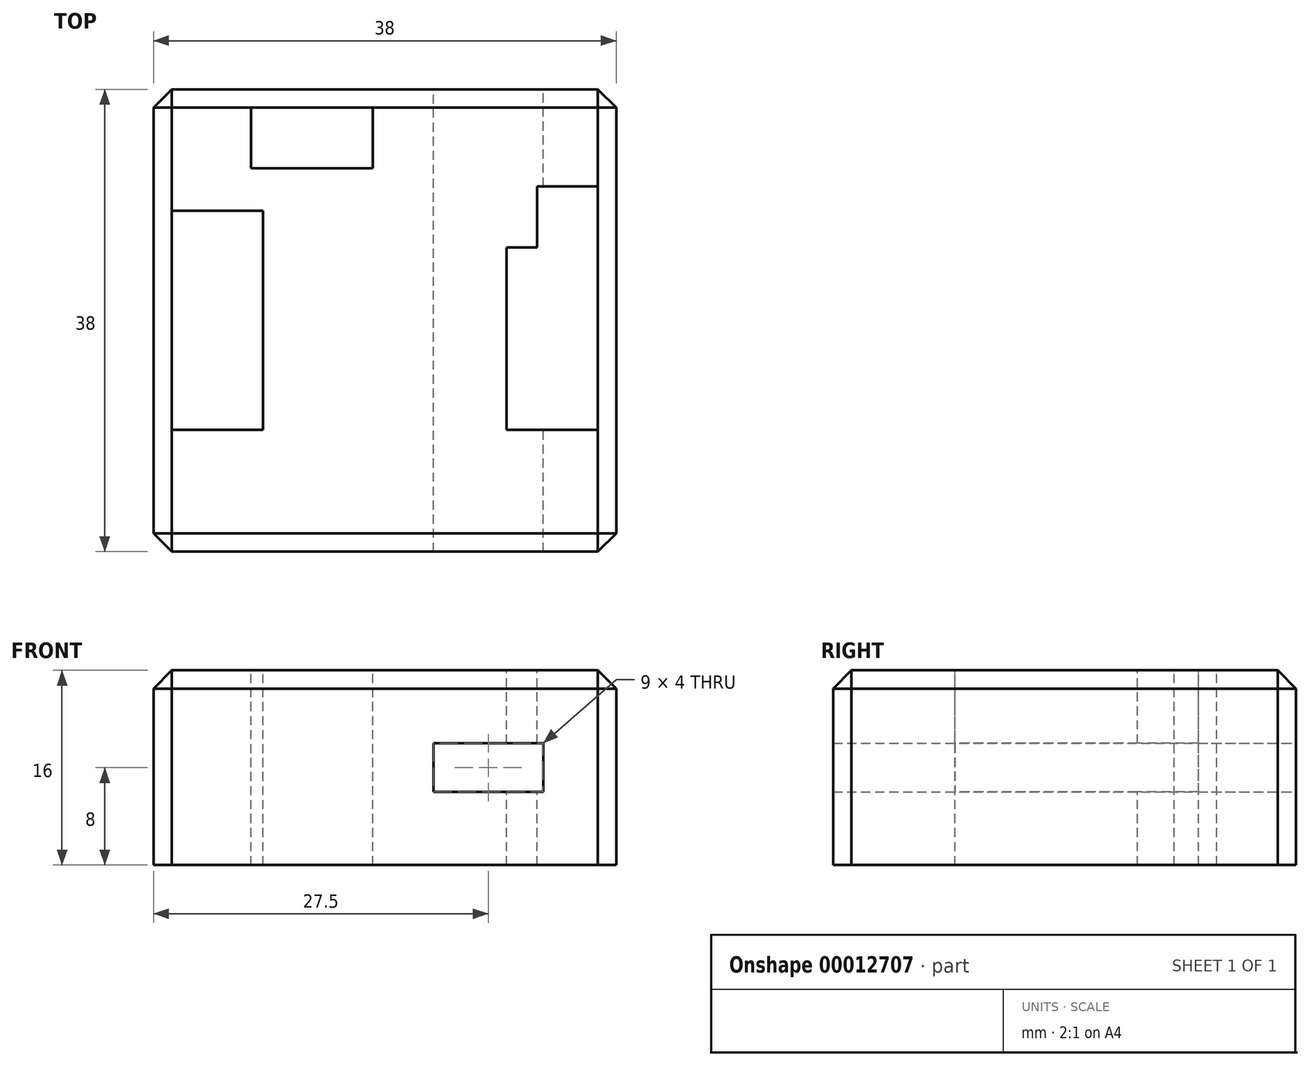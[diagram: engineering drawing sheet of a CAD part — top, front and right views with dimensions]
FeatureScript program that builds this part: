
annotation { "Feature Type Name" : "Feature", "Feature Type Description" : "" }
export const myFeature = defineFeature(function(context is Context, id is Id, definition is map)
    precondition{}
    {
        {
            var Q0;
            Q0=qCreatedBy(makeId("Top.planeOp"),FACE);
            var sketch = newSketch(context, id + "F0", { "sketchPlane" : qUnion([Q0])});
            skLineSegment(sketch, "E0.rect.bottom", {"start": v(19, 19) * mm, "end": v(-19, 19) * mm});
            skLineSegment(sketch, "E0.rect.top", {"start": v(19, -19) * mm, "end": v(-19, -19) * mm});
            skLineSegment(sketch, "E0.rect.left", {"start": v(19, 19) * mm, "end": v(19, -19) * mm});
            skLineSegment(sketch, "E0.rect.right", {"start": v(-19, 19) * mm, "end": v(-19, -19) * mm});
            skPoint(sketch, "E0.rect.middle", {"position": v(0, 0) * mm});
            skSolve(sketch);
        }
        {
            var Q0;
            Q0=qSketchRegion(id+"F0",true);
            extrude(context, id + "F1", {"entities" : qUnion([Q0]), "depth" : 16 * mm});
        }
        {
            var Q0;
            Q0=makeQuery(id+"F1.opExtrude","CAP_FACE",FACE,{"disambiguationData":[OSD([sQuery(id+"F0.wireOp",EDGE,"E0.rect.bottom"),sQuery(id+"F0.wireOp",EDGE,"E0.rect.top"),sQuery(id+"F0.wireOp",EDGE,"E0.rect.left"),sQuery(id+"F0.wireOp",EDGE,"E0.rect.right")])],"isStart":false});
            var Q1;
            Q1=makeQuery(id+"F1.opExtrude","SWEPT_EDGE",EDGE,{"disambiguationData":[OSD([sQuery(id+"F0.wireOp",EDGE,"E0.rect.top"),sQuery(id+"F0.wireOp",EDGE,"E0.rect.left")])]});
            var Q2;
            Q2=makeQuery(id+"F1.opExtrude","SWEPT_EDGE",EDGE,{"disambiguationData":[OSD([sQuery(id+"F0.wireOp",EDGE,"E0.rect.top"),sQuery(id+"F0.wireOp",EDGE,"E0.rect.right")])]});
            var Q3;
            Q3=makeQuery(id+"F1.opExtrude","SWEPT_EDGE",EDGE,{"disambiguationData":[OSD([sQuery(id+"F0.wireOp",EDGE,"E0.rect.bottom"),sQuery(id+"F0.wireOp",EDGE,"E0.rect.left")])]});
            var Q4;
            Q4=makeQuery(id+"F1.opExtrude","SWEPT_EDGE",EDGE,{"disambiguationData":[OSD([sQuery(id+"F0.wireOp",EDGE,"E0.rect.bottom"),sQuery(id+"F0.wireOp",EDGE,"E0.rect.right")])]});
            chamfer(context, id + "F2", {"entities" : qUnion([Q0, Q1, Q2, Q3, Q4]), "width" : 1.5 * mm, "tangentPropagation" : true});
        }
        {
            var Q0;
            Q0=makeQuery(id+"F1.opExtrude","SWEPT_FACE",FACE,{"disambiguationData":[OSD([sQuery(id+"F0.wireOp",EDGE,"E0.rect.bottom")])]});
            var sketch = newSketch(context, id + "F3", { "sketchPlane" : qUnion([Q0])});
            skLineSegment(sketch, "E1.bottom", {"start": v(-13, 6) * mm, "end": v(-4, 6) * mm});
            skLineSegment(sketch, "E1.top", {"start": v(-13, 10) * mm, "end": v(-4, 10) * mm});
            skLineSegment(sketch, "E1.left", {"start": v(-13, 6) * mm, "end": v(-13, 10) * mm});
            skLineSegment(sketch, "E1.right", {"start": v(-4, 6) * mm, "end": v(-4, 10) * mm});
            skSolve(sketch);
        }
        {
            var Q0;
            Q0=makeQuery(id+"F3.imprint","IMPRINT",FACE,{"disambiguationData":[TD([[makeQuery(id+"F3.imprint","IMPRINT",EDGE,{"derivedFrom":sQuery(id+"F3.wireOp",EDGE,"E1.bottom")}),1.0]])]});
            extrude(context, id + "F4", {"entities" : qUnion([Q0]), "operationType" : NewBodyOperationType.REMOVE, "endBound" : BoundingType.UP_TO_NEXT, "oppositeDirection" : true, "depth" : 25 * mm});
        }
        {
            var Q0;
            Q0=makeQuery(id+"F1.opExtrude","CAP_FACE",FACE,{"disambiguationData":[OSD([sQuery(id+"F0.wireOp",EDGE,"E0.rect.bottom"),sQuery(id+"F0.wireOp",EDGE,"E0.rect.top"),sQuery(id+"F0.wireOp",EDGE,"E0.rect.left"),sQuery(id+"F0.wireOp",EDGE,"E0.rect.right")])],"isStart":false});
            var sketch = newSketch(context, id + "F5", { "sketchPlane" : qUnion([Q0])});
            skLineSegment(sketch, "E2", {"start": v(17.5, -9) * mm, "end": v(10, -9) * mm});
            skLineSegment(sketch, "E3", {"start": v(10, -9) * mm, "end": v(10, 6) * mm});
            skLineSegment(sketch, "E4", {"start": v(10, 6) * mm, "end": v(12.5, 6) * mm});
            skLineSegment(sketch, "E5", {"start": v(12.5, 6) * mm, "end": v(12.5, 11) * mm});
            skLineSegment(sketch, "E6", {"start": v(12.5, 11) * mm, "end": v(17.5, 11) * mm});
            skLineSegment(sketch, "E7", {"start": v(17.5, 11) * mm, "end": v(17.5, -9) * mm});
            skLineSegment(sketch, "E8", {"start": v(-17.5, -9) * mm, "end": v(-10, -9) * mm});
            skLineSegment(sketch, "E9", {"start": v(-10, -9) * mm, "end": v(-10, 9) * mm});
            skLineSegment(sketch, "E10", {"start": v(-10, 9) * mm, "end": v(-17.5, 9) * mm});
            skLineSegment(sketch, "E11", {"start": v(-17.5, 9) * mm, "end": v(-17.5, -9) * mm});
            skLineSegment(sketch, "E12", {"start": v(-11, 17.5) * mm, "end": v(-11, 12.5) * mm});
            skLineSegment(sketch, "E13", {"start": v(-11, 12.5) * mm, "end": v(-1, 12.5) * mm});
            skLineSegment(sketch, "E14", {"start": v(-1, 12.5) * mm, "end": v(-1, 17.5) * mm});
            skLineSegment(sketch, "E15", {"start": v(-1, 17.5) * mm, "end": v(-11, 17.5) * mm});
            skSolve(sketch);
        }
        {
            var Q0;
            Q0=makeQuery(id+"F5.imprint","IMPRINT",FACE,{"disambiguationData":[TD([[makeQuery(id+"F5.imprint","IMPRINT",EDGE,{"derivedFrom":sQuery(id+"F5.wireOp",EDGE,"E2")}),-1.0]])]});
            var Q1;
            Q1=makeQuery(id+"F5.imprint","IMPRINT",FACE,{"disambiguationData":[TD([[makeQuery(id+"F5.imprint","IMPRINT",EDGE,{"derivedFrom":sQuery(id+"F5.wireOp",EDGE,"E12")}),1.0]])]});
            var Q2;
            Q2=makeQuery(id+"F5.imprint","IMPRINT",FACE,{"disambiguationData":[TD([[makeQuery(id+"F5.imprint","IMPRINT",EDGE,{"derivedFrom":sQuery(id+"F5.wireOp",EDGE,"E8")}),1.0]])]});
            extrude(context, id + "F6", {"entities" : qUnion([Q0, Q1, Q2]), "operationType" : NewBodyOperationType.REMOVE, "endBound" : BoundingType.UP_TO_NEXT, "oppositeDirection" : true, "depth" : 25 * mm});
        }
    });
